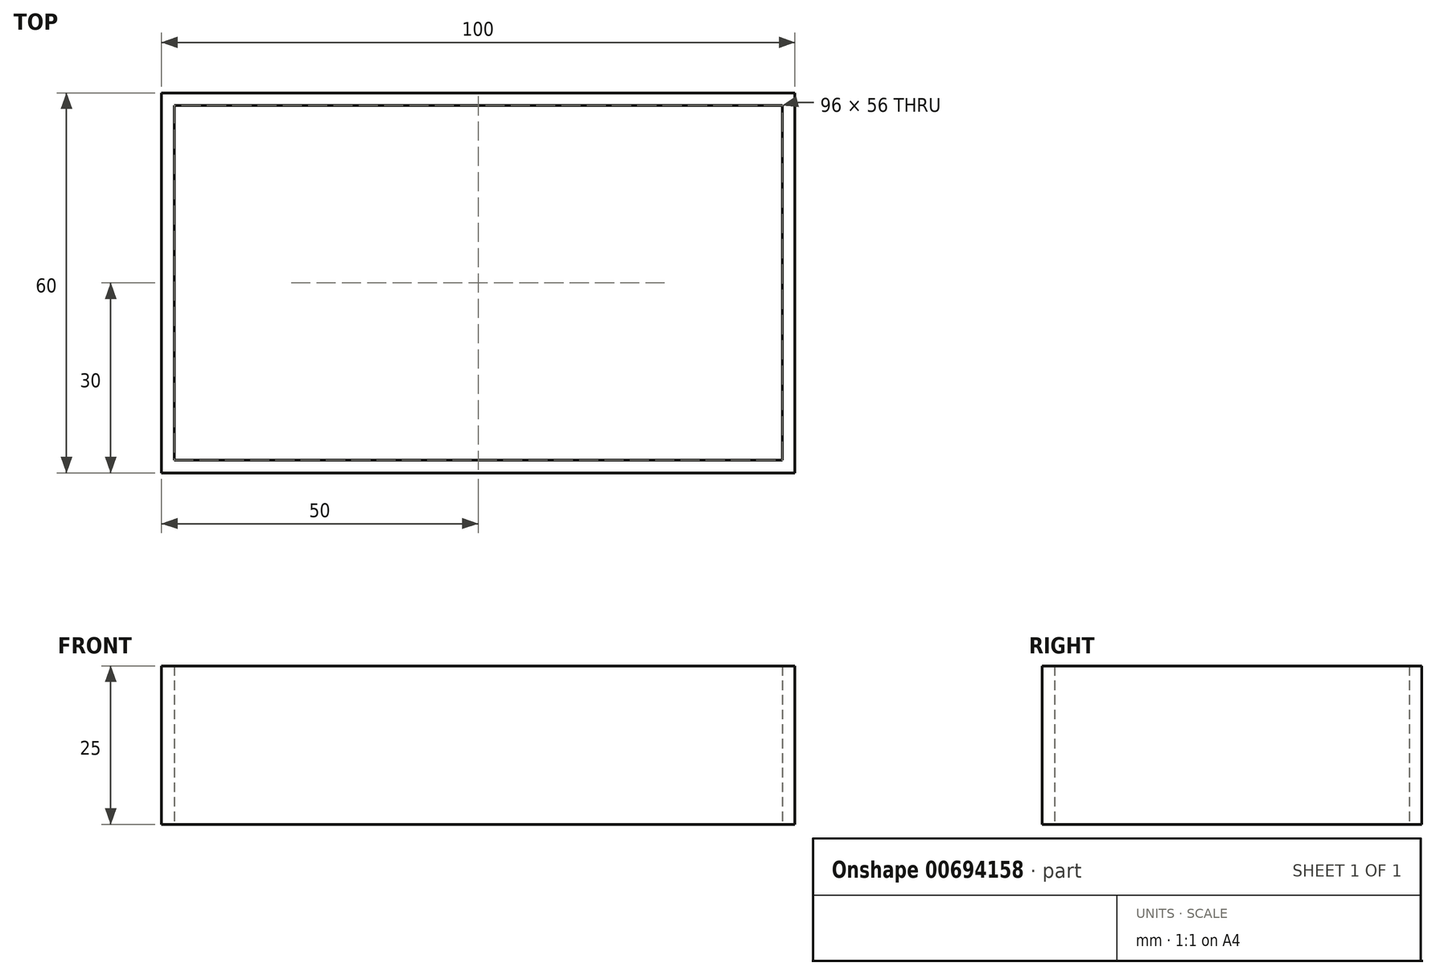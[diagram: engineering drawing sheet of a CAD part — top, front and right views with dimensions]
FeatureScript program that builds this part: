
annotation { "Feature Type Name" : "Feature", "Feature Type Description" : "" }
export const myFeature = defineFeature(function(context is Context, id is Id, definition is map)
    precondition{}
    {
        {
            var Q0;
            Q0=qCreatedBy(makeId("Top.planeOp"),FACE);
            var sketch = newSketch(context, id + "F0", { "sketchPlane" : qUnion([Q0])});
            skLineSegment(sketch, "E0.bottom", {"start": v(-50, -30) * mm, "end": v(50, -30) * mm});
            skLineSegment(sketch, "E0.top", {"start": v(-50, 30) * mm, "end": v(50, 30) * mm});
            skLineSegment(sketch, "E0.left", {"start": v(-50, -30) * mm, "end": v(-50, 30) * mm});
            skLineSegment(sketch, "E0.right", {"start": v(50, -30) * mm, "end": v(50, 30) * mm});
            skPoint(sketch, "E0.middle", {"position": v(0, 0) * mm});
            skLineSegment(sketch, "E1.bottom", {"start": v(48, -28) * mm, "end": v(-48, -28) * mm});
            skLineSegment(sketch, "E1.top", {"start": v(48, 28) * mm, "end": v(-48, 28) * mm});
            skLineSegment(sketch, "E1.left", {"start": v(48, -28) * mm, "end": v(48, 28) * mm});
            skLineSegment(sketch, "E1.right", {"start": v(-48, -28) * mm, "end": v(-48, 28) * mm});
            skSolve(sketch);
        }
        {
            var Q0;
            Q0 = qSketchRegion(id + "F0", true);
            extrude(context, id + "F1", {"entities" : qUnion([Q0]), "depth" : 25 * mm, "offsetDistance" : 25 * mm});
        }
    });
